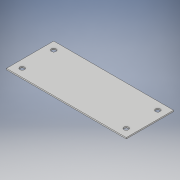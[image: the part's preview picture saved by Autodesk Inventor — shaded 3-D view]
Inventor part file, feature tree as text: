
AUTODESK INVENTOR PART (.ipt)
format: ipt  version: 2018 (Build 220112000, 112)  size: 103,424 bytes
history: native  units: in
note: dims shown in document units (in); Inventor stores cm internally (conversion verified against a paired STEP export)
features: extrude x2, sketch x2
ambient origin geometry x8: Origin, YZ Plane, XZ Plane, XY Plane, X Axis, Y Axis, Z Axis, Center Point
bodies: Solid1 (feature_tree)
feature tree (4):
  extrude  "Extrusion1"  Depth=1.1811in
  extrude  "Extrusion2"  Depth=0.031in
  sketch  "Sketch1"  dims[d0=2.9921in d1=1.1811in]
  sketch  "Sketch2"  dims[d2=0.031in d3=0.0in d4=0.1181in d5=0.1181in d6=0.1181in d7=0.1181in d8=0.0in d9=0.0in]
